# Revit family: Haworth_HushOffice_Mikomax_HushMeet.L3_AP_PRELIMINARY
name_source: partatom
category: Casework
units: mm (PartAtom-declared; Revit-internal decimal feet)

## family parameters
Always vertical = Yes
Cut with Voids When Loaded = No
OmniClass Number = 23.40.35.00
OmniClass Title = Casework
Room Calculation Point = Yes
Shared = No
Work Plane-Based = No

## types (1)
- Hush Meet L3
    Assembly Code = E2010200
    Back glass colour = Haworth _ Glass _ Clear
    Case = Haworth _ Laminate _ Undecided
    Construction Type = Defined construction
    Depth = 2700 mm  [stored 8.85827 ft]
    Description = Haworth - Hush Office - Mikomax - HushMeet - L3
    Door Glass = Haworth _ Glass _ Clear
    E AU = Power module : AU Type (2 x electric, 2 x RJ45, 2 x USB C, 2 x USB A) - black
    E CH = Power module : CH (2 x electric, 2 x USB, 2 x RJ45)
    E CT = Interior : conference table
    E DE = Power module : DE (2 x electric, 2 x USB, 2 x RJ45)
    E DK = Power module : DK (2 x electric, 2 x USB, 2 x RJ45)
    E GB = Power module : GB (2 x electric, 2 x USB, 2 x RJ45)
    E GB2 = Power module : GB Type (2 x electric, 2 x RJ45, 2 x USB C, 2 x USB A) - black
    E PL/FR = Power module : PL/FR (2 x  electric, 2 x USB, 2 x RJ45)
    E PL/FR2 = Power module : PL/FR Type (1 x electric,1 x USB A,1 x  USB C,1 x RJ45) - black
    E US = Power module : US Type (2 x electric, 2 x RJ45, 2 x USB C, 2 x USB A) - black
    Fabric = Haworth _ Fabric _ Undecided
    Finish = Defined materials
    Frame = Haworth _ Paint _ Undecided
    Handle and hinges = Haworth _ Metal _ Undecided
    Height = 2200 mm  [stored 7.21785 ft]
    IfcExportAs = IfcFurniture
    Manufacturer = Haworth
    Middle column = Haworth _ Laminate _ Undecided
    Model = XCMMHML3
    Revision Number = 1
    Size = Verify Final Dim. w/ Haworth
    Sustainability Info = https://www.haworth.com
    Type Image = Haworth_HushAccess.L.jpg
    URL = https://www.haworth.com
    URL - Product = https://www.haworth.com
    Warranty = https://cdn.shopify.com
    Width = 2600 mm  [stored 8.53018 ft]

note: [stored X ft] marks values corroborated as IEEE doubles in the binary element streams (Revit-internal decimal feet)

## geometry (parser evidence)
native form markers: Sweep x53
no freeform markers — native parametric forms only
